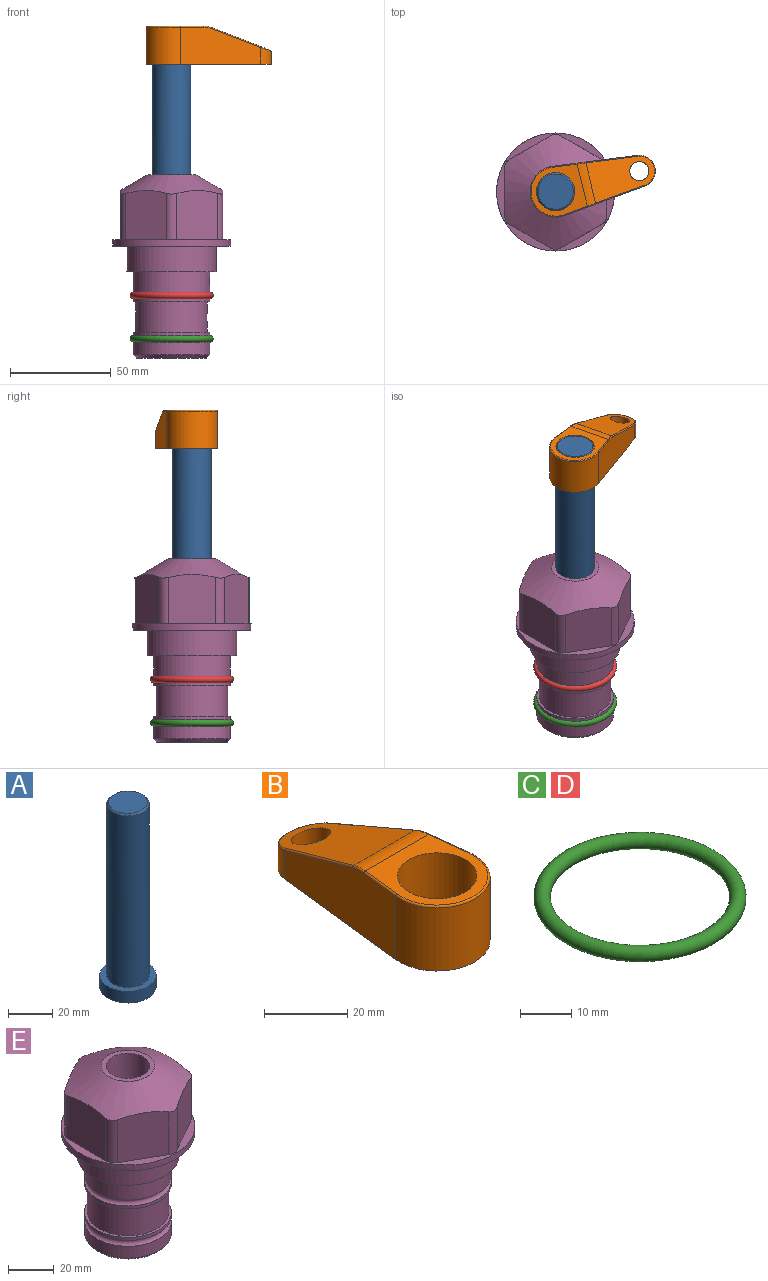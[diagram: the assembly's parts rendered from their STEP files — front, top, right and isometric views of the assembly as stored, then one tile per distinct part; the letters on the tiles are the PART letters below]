
ASSEMBLY  parts=5 mates=3
PART A: 6 faces, bbox 25.4x25.4x101.6 mm
  f0: plane 17.46x17.46mm, normal (0,0,1), area 239.5mm2, adj f5
  f1: plane 25.4x25.4mm, normal (0,0,-1), area 506.7mm2, adj f2
  f2: cylinder r=12.7mm len=25.4mm, axis (0,0,1), area 506.7mm2, adj f1,f3
  f3: plane 25.4x25.4mm, normal (0,0,1), area 221.7mm2, adj f2,f4
  f4: cylinder r=9.53mm len=94.46mm, axis (0,0,1), area 5653mm2, adj f3,f5
  f5: cone r=8.73mm half-angle=45deg, axis (0,0,-1), area 64.4mm2, adj f0,f4
PART B: 44 faces, bbox 27.5x64.5x19.1 mm
  f0: plane 2.3x0.95mm, normal (0,0,-1), area 1mm2, adj f25,f30,f34
  f1: plane 63.5x25.4mm, normal (0,0,-1), area 561.7mm2, adj f2,f3,f4,f5,f6,f7,f19,f20
  f2: cylinder r=12.7mm len=25.4mm, axis (0,0,-1), area 792.2mm2, adj f1,f3,f5,f13
  f3: plane 42.33x18.54mm, normal (0.99,0.11,0), area 647mm2, adj f1,f2,f4,f11,f12,f14
  f4: cylinder r=7.94mm len=15.78mm, axis (0,0,-1), area 158.6mm2, adj f1,f3,f5,f16
  f5: plane 42.33x18.54mm, normal (-0.99,0.11,0), area 647mm2, adj f1,f2,f4,f15,f17,f18
  f6: cylinder r=9.53mm len=19.05mm, axis (0,0,-1), area 1140.1mm2, adj f1,f8
  f7: cylinder r=4.76mm len=10.98mm, axis (0,0,-1), area 276.1mm2, adj f1,f9
  f8: plane 25.83x24.38mm, normal (0,0,1), area 262.2mm2, adj f6,f10,f11,f13,f15
  f9: plane 32.49x20.55mm, normal (0,0.34,0.94), area 489.9mm2, adj f7,f10,f14,f16,f18
  f10: cylinder r=12.7mm len=21.49mm, axis (-1,0,0), area 93.2mm2, adj f8,f9,f12,f17
  f11: cylinder r=0.51mm len=12.34mm, axis (0.11,-0.99,0), area 9.9mm2, adj f3,f8,f12,f13
  f12: bspline ~7.62x1.64mm, area 3.5mm2, adj f3,f10,f11,f14
  f13: torus R=12.19mm, axis (0,0,1), area 33.6mm2, adj f2,f8,f11,f15
  f14: cylinder r=0.51mm len=26.01mm, axis (0.1,-0.93,0.34), area 21.6mm2, adj f3,f9,f12,f16
  f15: cylinder r=0.51mm len=12.34mm, axis (0.11,0.99,0), area 9.9mm2, adj f5,f8,f13,f17
  f16: bspline ~15.78x7.05mm, area 15.7mm2, adj f4,f9,f14,f18
  f17: bspline ~7.62x1.64mm, area 3.5mm2, adj f5,f10,f15,f18
  f18: cylinder r=0.51mm len=26.01mm, axis (0.1,0.93,-0.34), area 21.6mm2, adj f5,f9,f16,f17
  f19: plane 21.6x14.29mm, normal (-0.99,-0.11,0), area 242.6mm2, adj f1,f26,f28,f34,f36,f38
  f20: plane 21.6x14.29mm, normal (0.99,-0.11,0), area 242.6mm2, adj f1,f27,f29,f37,f39,f41
  f21: cylinder r=12.7mm len=14.29mm, axis (0,0,-1), area 173.2mm2, adj f1,f26,f27,f30,f31,f33
  f22: cylinder r=7.94mm len=7.63mm, axis (0,0,-1), area 53.8mm2, adj f1,f28,f29,f42
  f23: plane 2.3x0.95mm, normal (0,0,-1), area 1mm2, adj f25,f33,f37
  f24: plane 17.94x12.32mm, normal (0,-0.34,-0.94), area 191.2mm2, adj f25,f38,f41,f42
  f25: cylinder r=9.53mm len=12.93mm, axis (-1,0,0), area 37.5mm2, adj f0,f23,f24,f31,f36,f39
  f26: cylinder r=1.59mm len=14.29mm, axis (0,0,-1), area 49mm2, adj f1,f19,f21,f32
  f27: cylinder r=1.59mm len=14.29mm, axis (0,0,-1), area 49mm2, adj f1,f20,f21,f35
  f28: cylinder r=1.59mm len=7.28mm, axis (0,0,-1), area 22.1mm2, adj f1,f19,f22,f40
  f29: cylinder r=1.59mm len=7.28mm, axis (0,0,-1), area 22.1mm2, adj f1,f20,f22,f43
  f30: torus R=14.29mm, axis (0,0,1), area 5.8mm2, adj f0,f21,f31,f32
  f31: bspline ~11.06x2.73mm, area 20.8mm2, adj f21,f25,f30,f33
  f32: sphere r=1.59mm, area 5.4mm2, adj f26,f30,f34
  f33: torus R=14.29mm, axis (0,0,1), area 5.8mm2, adj f21,f23,f31,f35
  f34: cylinder r=1.59mm len=1.68mm, axis (-0.11,0.99,0), area 2.4mm2, adj f0,f19,f32,f36
  f35: sphere r=1.59mm, area 5.4mm2, adj f27,f33,f37
  f36: bspline ~5.82x2.33mm, area 7.7mm2, adj f19,f25,f34,f38
  f37: cylinder r=1.59mm len=1.68mm, axis (0.11,0.99,0), area 2.4mm2, adj f20,f23,f35,f39
  f38: cylinder r=1.59mm len=18.33mm, axis (0.1,-0.93,0.34), area 46.7mm2, adj f19,f24,f36,f40
  f39: bspline ~5.82x2.33mm, area 7.7mm2, adj f20,f25,f37,f41
  f40: sphere r=1.59mm, area 3.6mm2, adj f28,f38,f42
  f41: cylinder r=1.59mm len=18.33mm, axis (0.1,0.93,-0.34), area 46.7mm2, adj f20,f24,f39,f43
  f42: bspline ~8.31x1.84mm, area 15.3mm2, adj f22,f24,f40,f43
  f43: sphere r=1.59mm, area 3.6mm2, adj f29,f41,f42
PART C: 1 faces, bbox 44.7x44.7x3.2 mm
  f0: torus R=19.05mm, axis (0,0,1), area 1193.9mm2
PART D: same geometry as C
PART E: 36 faces, bbox 58.7x58.7x91.2 mm
  f0: cylinder r=17.78mm len=35.56mm, axis (0,0,1), area 1670.8mm2, adj f23,f24,f31
  f1: cylinder r=19.05mm len=38.1mm, axis (0,0,1), area 1191.9mm2, adj f26,f27,f30
  f2: plane 58.66x58.66mm, normal (0,0,-1), area 1150.6mm2, adj f3,f28
  f3: cylinder r=29.33mm len=58.66mm, axis (0,0,-1), area 585.1mm2, adj f2,f4
  f4: plane 58.66x58.66mm, normal (0,0,1), area 475.9mm2, adj f3,f5,f6,f7,f8,f9,f10,f11
  f5: plane 24.5x20.32mm, normal (-0.5,0.87,0), area 562.8mm2, adj f4,f15,f16,f17
  f6: plane 24.5x20.32mm, normal (0.5,0.87,0), area 562.8mm2, adj f4,f14,f15,f17
  f7: plane 24.5x23.48mm, normal (1,0,0), area 562.8mm2, adj f4,f13,f14,f17
  f8: plane 24.5x20.32mm, normal (0.5,-0.87,0), area 562.8mm2, adj f4,f12,f13,f17
  f9: plane 24.5x20.32mm, normal (-0.5,-0.87,0), area 562.8mm2, adj f4,f11,f12,f17
  f10: plane 24.5x23.48mm, normal (-1,0,0), area 562.8mm2, adj f4,f11,f16,f17
  f11: cylinder r=5.08mm len=23.01mm, axis (0,0,-1), area 121.2mm2, adj f4,f9,f10,f17
  f12: cylinder r=5.08mm len=23.01mm, axis (0,0,-1), area 121.2mm2, adj f4,f8,f9,f17
  f13: cylinder r=5.08mm len=23.01mm, axis (0,0,-1), area 121.2mm2, adj f4,f7,f8,f17
  f14: cylinder r=5.08mm len=23.01mm, axis (0,0,-1), area 121.2mm2, adj f4,f6,f7,f17
  f15: cylinder r=5.08mm len=23.01mm, axis (0,0,-1), area 121.2mm2, adj f4,f5,f6,f17
  f16: cylinder r=5.08mm len=23.01mm, axis (0,0,-1), area 121.2mm2, adj f4,f5,f10,f17
  f17: cone r=11.73mm half-angle=60deg, axis (0,0,-1), area 2071.8mm2, adj f5,f6,f7,f8,f9,f10,f11,f12
  f18: plane 23.46x23.46mm, normal (0,0,1), area 147.4mm2, adj f17,f35
  f19: plane 34.93x34.93mm, normal (0,0,-1), area 958mm2, adj f29
  f20: cylinder r=19.05mm len=38.1mm, axis (0,0,1), area 760.1mm2, adj f21,f29
  f21: torus R=19.05mm, axis (0,0,1), area 565.3mm2, adj f20,f22
  f22: cylinder r=19.05mm len=38.1mm, axis (0,0,1), area 190mm2, adj f21,f23
  f23: plane 38.1x38.1mm, normal (0,0,1), area 146.9mm2, adj f0,f22
  f24: plane 38.1x38.1mm, normal (0,0,-1), area 146.9mm2, adj f0,f25
  f25: cylinder r=19.05mm len=38.1mm, axis (0,0,1), area 190mm2, adj f24,f26
  f26: torus R=19.05mm, axis (0,0,1), area 565.3mm2, adj f1,f25
  f27: plane 44.45x44.45mm, normal (0,0,-1), area 411.7mm2, adj f1,f28
  f28: cylinder r=22.23mm len=44.45mm, axis (0,0,1), area 1773.5mm2, adj f2,f27
  f29: cone r=19.05mm half-angle=45deg, axis (0,0,1), area 257.5mm2, adj f19,f20
  f30: cylinder r=3.17mm len=6.75mm, axis (-1,0,0), area 128mm2, adj f1,f33
  f31: cylinder r=3.17mm len=6.35mm, axis (-1,0,0), area 102.5mm2, adj f0,f33
  f32: plane 25.4x25.4mm, normal (0,0,1), area 506.7mm2, adj f33
  f33: cylinder r=12.7mm len=66.42mm, axis (0,0,-1), area 5236.2mm2, adj f30,f31,f32,f34
  f34: cone r=9.53mm half-angle=30deg, axis (0,0,-1), area 443.4mm2, adj f33,f35
  f35: cylinder r=9.53mm len=19.05mm, axis (0,0,-1), area 849mm2, adj f18,f34
PLACE A rot(axis=(0,0,1),13.7deg) t=(0,0,35.74)mm
PLACE B rot(axis=(0,0,-1),76.3deg) t=(0,0,90.35)mm
PLACE C t=(0,0,-21.59)mm
PLACE D at identity
PLACE E at identity fixed
MATE fastened C.f0 <-> E.f0  axis (0,0,1) through (0,0,-46.1)mm
MATE cylindrical A.f2 <-> E.f0  axis (0,0,1) through (0,0,61.37)mm
MATE fastened B.f2 <-> A.f2  axis (0,0,1) through (0,0,109.4)mm
